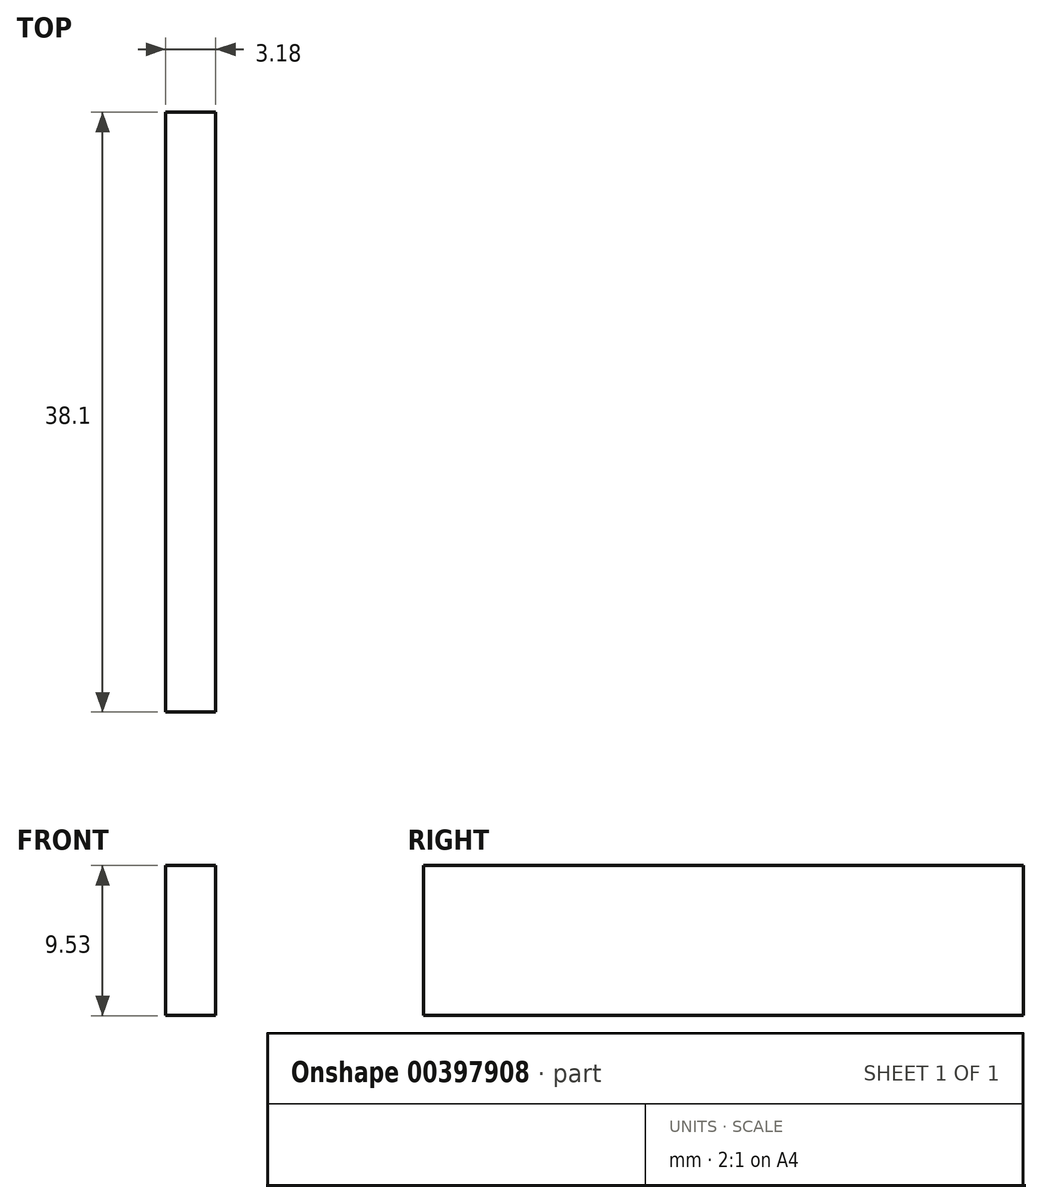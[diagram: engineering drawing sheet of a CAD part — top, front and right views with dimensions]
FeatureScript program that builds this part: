
annotation { "Feature Type Name" : "Feature", "Feature Type Description" : "" }
export const myFeature = defineFeature(function(context is Context, id is Id, definition is map)
    precondition{}
    {
        {
            var Q0;
            Q0=qCreatedBy(makeId("Top.planeOp"),FACE);
            var sketch = newSketch(context, id + "F0", { "sketchPlane" : qUnion([Q0])});
            skLineSegment(sketch, "E0.bottom", {"start": v(1.59, -19.05) * mm, "end": v(-1.59, -19.05) * mm});
            skLineSegment(sketch, "E0.top", {"start": v(1.59, 19.05) * mm, "end": v(-1.59, 19.05) * mm});
            skLineSegment(sketch, "E0.left", {"start": v(1.59, -19.05) * mm, "end": v(1.59, 19.05) * mm});
            skLineSegment(sketch, "E0.right", {"start": v(-1.59, -19.05) * mm, "end": v(-1.59, 19.05) * mm});
            skPoint(sketch, "E0.middle", {"position": v(0, 0) * mm});
            skSolve(sketch);
        }
        {
            var Q0;
            Q0=makeQuery(id+"F0.imprint","IMPRINT",FACE,{"disambiguationData":[TD([[makeQuery(id+"F0.imprint","IMPRINT",EDGE,{"derivedFrom":sQuery(id+"F0.wireOp",EDGE,"E0.bottom")}),-1.0]])]});
            extrude(context, id + "F1", {"entities" : qUnion([Q0]), "oppositeDirection" : true, "depth" : 9.52 * mm});
        }
    });
